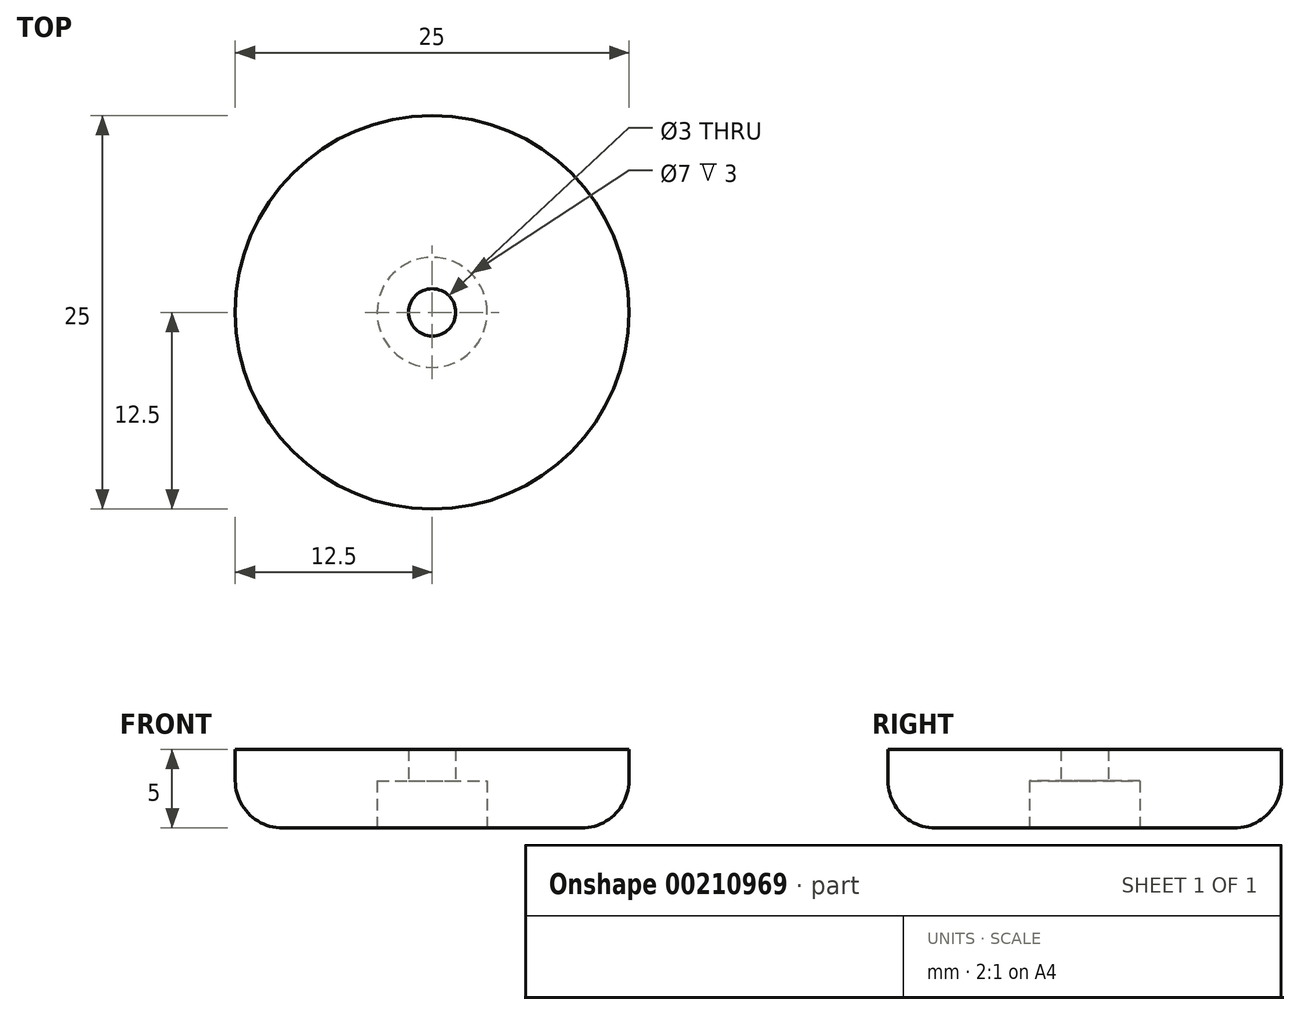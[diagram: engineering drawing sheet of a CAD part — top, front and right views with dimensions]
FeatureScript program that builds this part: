
annotation { "Feature Type Name" : "Feature", "Feature Type Description" : "" }
export const myFeature = defineFeature(function(context is Context, id is Id, definition is map)
    precondition{}
    {
        {
            assignVariable(context, id + "F0", {"name" : "mnt_hole", "anyValue" : 3});
        }
        {
            assignVariable(context, id + "F1", {"name" : "fillet_radius", "anyValue" : 3});
        }
        {
            assignVariable(context, id + "F2", {"name" : "counterbore_dia", "anyValue" : 7});
        }
        {
            assignVariable(context, id + "F3", {"name" : "counterbore_depth", "anyValue" : 3});
        }
        {
            assignVariable(context, id + "F4", {"name" : "height", "anyValue" : 5});
        }
        {
            var Q0;
            Q0=qCreatedBy(makeId("Top.planeOp"),FACE);
            var sketch = newSketch(context, id + "F5", { "sketchPlane" : qUnion([Q0])});
            skCircle(sketch, "E0", {"center": v(0, 0) * mm, "radius": 12.5 * mm});
            skSolve(sketch);
        }
        {
            var Q0;
            Q0 = qSketchRegion(id + "F5", true);
            extrude(context, id + "F6", {"entities" : qUnion([Q0]), "depth" : (getVariable(context, 'height')) * mm});
        }
        {
            var Q0;
            Q0=sQuery(id+"F5.wireOp",VERTEX,"E0.center");
            var Q1;
            Q1=makeQuery(id+"F6.opExtrude","SWEPT_BODY",BODY,{"disambiguationData":[OSD([sQuery(id+"F5.wireOp",EDGE,"E0")])]});
            hole(context, id + "F7", {"style" : HoleStyle.C_BORE, "endStyle" : HoleEndStyle.THROUGH, "oppositeDirection" : true, "holeDiameter" : getVariable(context, 'mnt_hole') * mm, "cBoreDiameter" : (getVariable(context, 'counterbore_dia')) * mm, "cBoreDepth" : (getVariable(context, 'counterbore_depth')) * mm, "startFromSketch" : true, "locations" : qUnion([Q0]), "scope" : qUnion([Q1]), "isTappedThrough" : true});
        }
        {
            var Q0;
            Q0=makeQuery(id+"F6.opExtrude","CAP_EDGE",EDGE,{"disambiguationData":[OSD([sQuery(id+"F5.wireOp",EDGE,"E0")])],"isStart":true});
            fillet(context, id + "F8", {"entities" : qUnion([Q0]), "radius" : (getVariable(context, 'fillet_radius')) * mm, "tangentPropagation" : true, "allowEdgeOverflow" : false});
        }
    });
